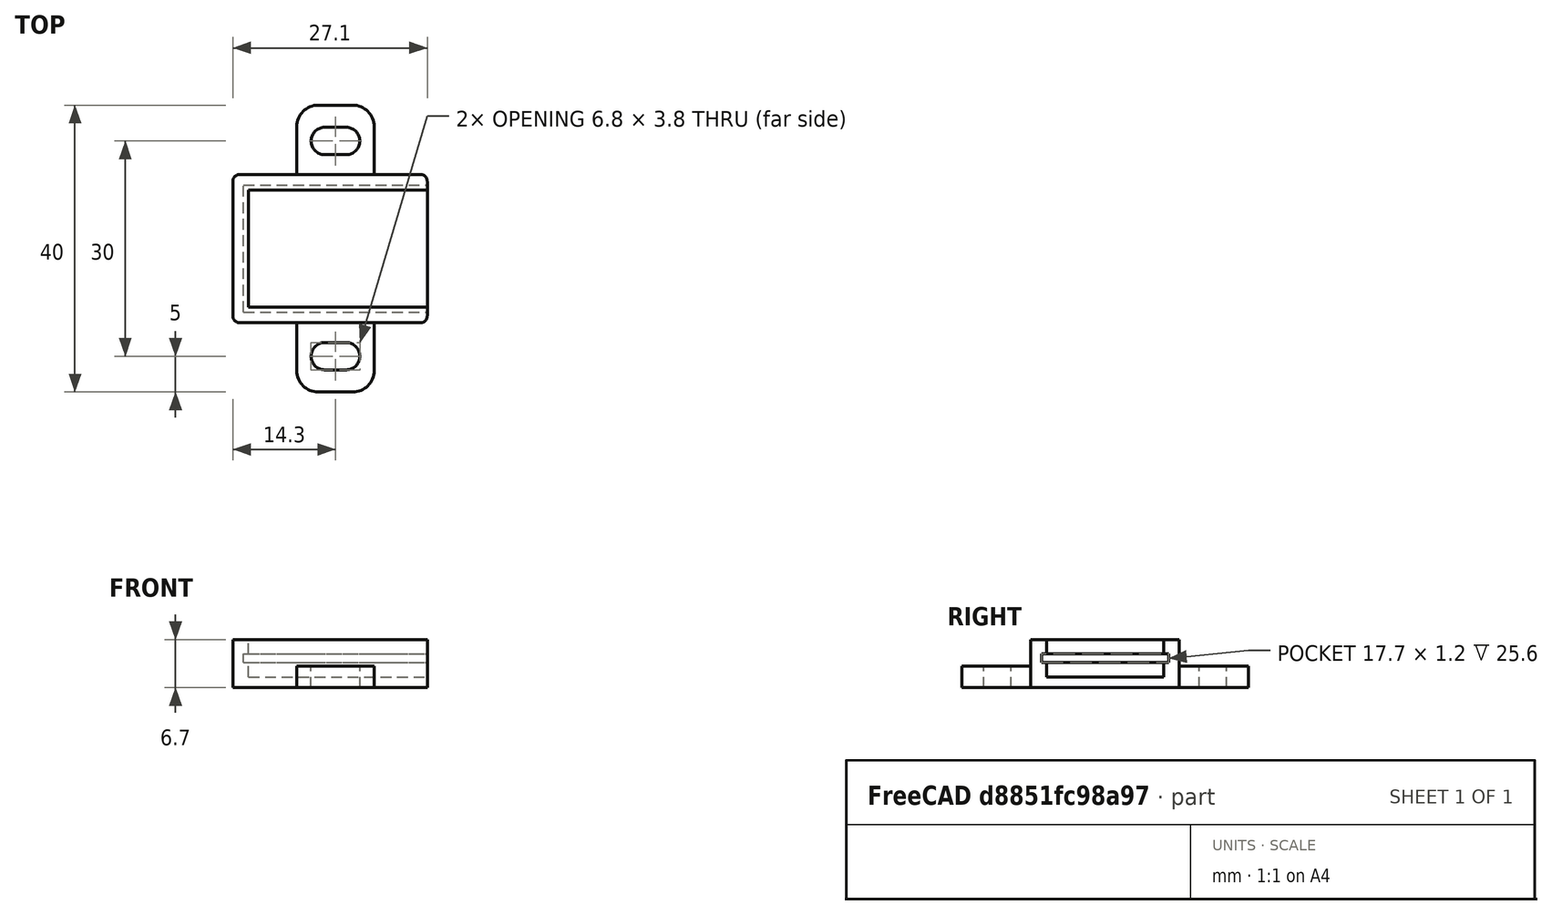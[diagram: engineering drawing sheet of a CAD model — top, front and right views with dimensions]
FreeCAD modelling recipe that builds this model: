
FCSTD DOCUMENT  (FreeCAD 0.18.4R)
Label: charger_tp5100
License: FreeArt
LicenseURL: http://artlibre.org/licence/lal
objects: Part::Box×3, Part::MultiFuse×2, Spreadsheet::Sheet×1, Part::Fillet×1, Part::Feature×1, Part::Cut×1, App::Part×1
note: 8 computed .brp shape members not serialized (recipe doc carries the construction recipe); baked Part::Feature solids carry a one-line shape summary decoded from their .brp

FEATURE [Spreadsheet::Sheet] Spreadsheet  label="p"
  cells = A1=pcb_x; B1(pcb_x)=25.6; A2=pcb_y; B2(pcb_y)=17.7; A3=pcb_z; B3(pcb_z)=1.2; A4=pcb_under; B4(pcb_under)=2; A5=side_wall; B5(side_wall)=1.5; A6=pcb_side_lane; B6(pcb_side_lane)=0.7; A7=bottom_wall; B7(bottom_wall)=1.5; A8=pcb_above; B8(pcb_above)=2
FEATURE [Part::Box] Box  label="external cube"
  AttacherType = Attacher::AttachEngine3D
  Height = 6.7
  Length = 27.1
  Width = 20.7
  expr: Height = p.bottom_wall + p.pcb_under + p.pcb_z + p.pcb_above
  expr: Width = p.pcb_y + 2 * p.side_wall
  expr: Length = p.pcb_x + p.side_wall
FEATURE [Part::Box] Box006  label="internal cube"
  AttacherType = Attacher::AttachEngine3D
  Height = 5.2
  Length = 25.7
  Placement = pos=(2.2,2.2,1.5) rot=(0,0,1;0rad)
  Width = 16.3
  expr: Placement.Base.y = p.side_wall + p.pcb_side_lane
  expr: Placement.Base.x = p.side_wall + p.pcb_side_lane
  expr: Placement.Base.z = p.bottom_wall
  expr: Height = p.pcb_under + p.pcb_z + p.pcb_above
  expr: Width = p.pcb_y - 2 * p.pcb_side_lane
  expr: Length = p.pcb_x - 2 * p.pcb_side_lane + p.side_wall
FEATURE [Part::Box] Box007  label="pcb extract cube"
  AttacherType = Attacher::AttachEngine3D
  Height = 1.2
  Length = 25.6
  Placement = pos=(1.5,1.5,3.5) rot=(0,0,1;0rad)
  Width = 17.7
  expr: Placement.Base.y = p.side_wall
  expr: Placement.Base.x = p.side_wall
  expr: Length = p.pcb_x
  expr: Width = p.pcb_y
  expr: Placement.Base.z = p.bottom_wall + p.pcb_under
  expr: Height = p.pcb_z
FEATURE [Part::MultiFuse] Fusion  label="extract fusion"
  Shapes = -> [Box006,Box007]
FEATURE [Part::Fillet] Fillet  label="external fillet"
  Base = -> Box
  Edges = 4 edges r=1: [Edge1,Edge3,Edge5,Edge7]
FEATURE [Part::Feature] Cut002001  label="attach plane y dir001"
  shape: bbox 10.8 x 40 x 3 mm, 18 faces (baked)
FEATURE [Part::MultiFuse] Fusion001  label="solid fusion"
  Shapes = -> [Fillet,Cut002001]
FEATURE [Part::Cut] Cut  label="tp5100 cut"
  Base = -> Fusion001
  Tool = -> Fusion
FEATURE [App::Part] Part  label="tp5100 pcb box part"
  Group = -> [Box,Fillet,Fusion001,Fusion,Box007,Box006,Cut]
  Origin = -> Origin
